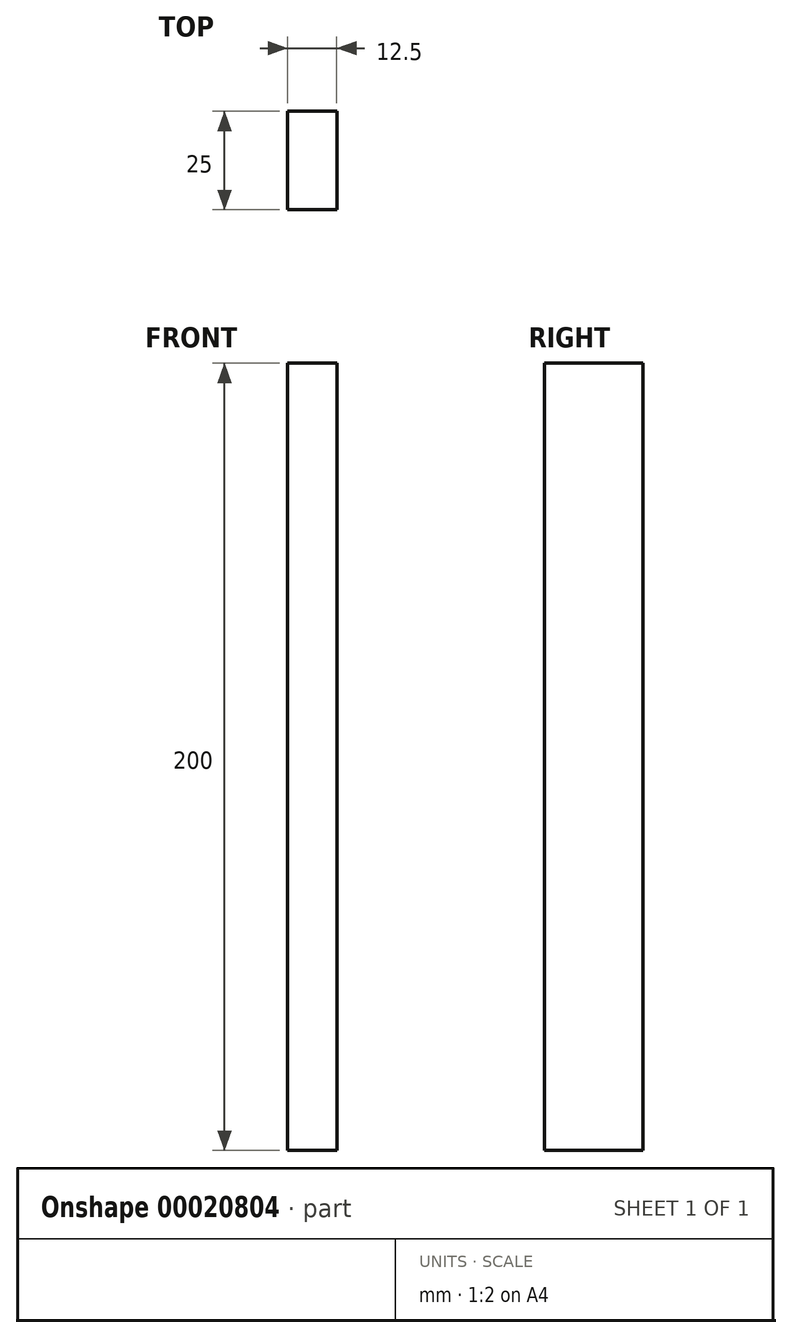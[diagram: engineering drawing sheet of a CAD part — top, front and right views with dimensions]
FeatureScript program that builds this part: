
annotation { "Feature Type Name" : "Feature", "Feature Type Description" : "" }
export const myFeature = defineFeature(function(context is Context, id is Id, definition is map)
    precondition{}
    {
        {
            var Q0;
            Q0=qCreatedBy(makeId("Front.planeOp"),FACE);
            var sketch = newSketch(context, id + "F0", { "sketchPlane" : qUnion([Q0])});
            skLineSegment(sketch, "E0.bottom", {"start": v(-44.77, 0) * mm, "end": v(-32.27, 0) * mm});
            skLineSegment(sketch, "E0.top", {"start": v(-44.77, 200) * mm, "end": v(-32.27, 200) * mm});
            skLineSegment(sketch, "E0.left", {"start": v(-44.77, 0) * mm, "end": v(-44.77, 200) * mm});
            skLineSegment(sketch, "E0.right", {"start": v(-32.27, 0) * mm, "end": v(-32.27, 200) * mm});
            skSolve(sketch);
        }
        {
            var Q0;
            Q0=makeQuery(id+"F0.imprint","IMPRINT",FACE,{"disambiguationData":[TD([[makeQuery(id+"F0.imprint","IMPRINT",EDGE,{"derivedFrom":sQuery(id+"F0.wireOp",EDGE,"E0.bottom")}),1.0]])]});
            extrude(context, id + "F1", {"entities" : qUnion([Q0]), "depth" : 25 * mm});
        }
    });
